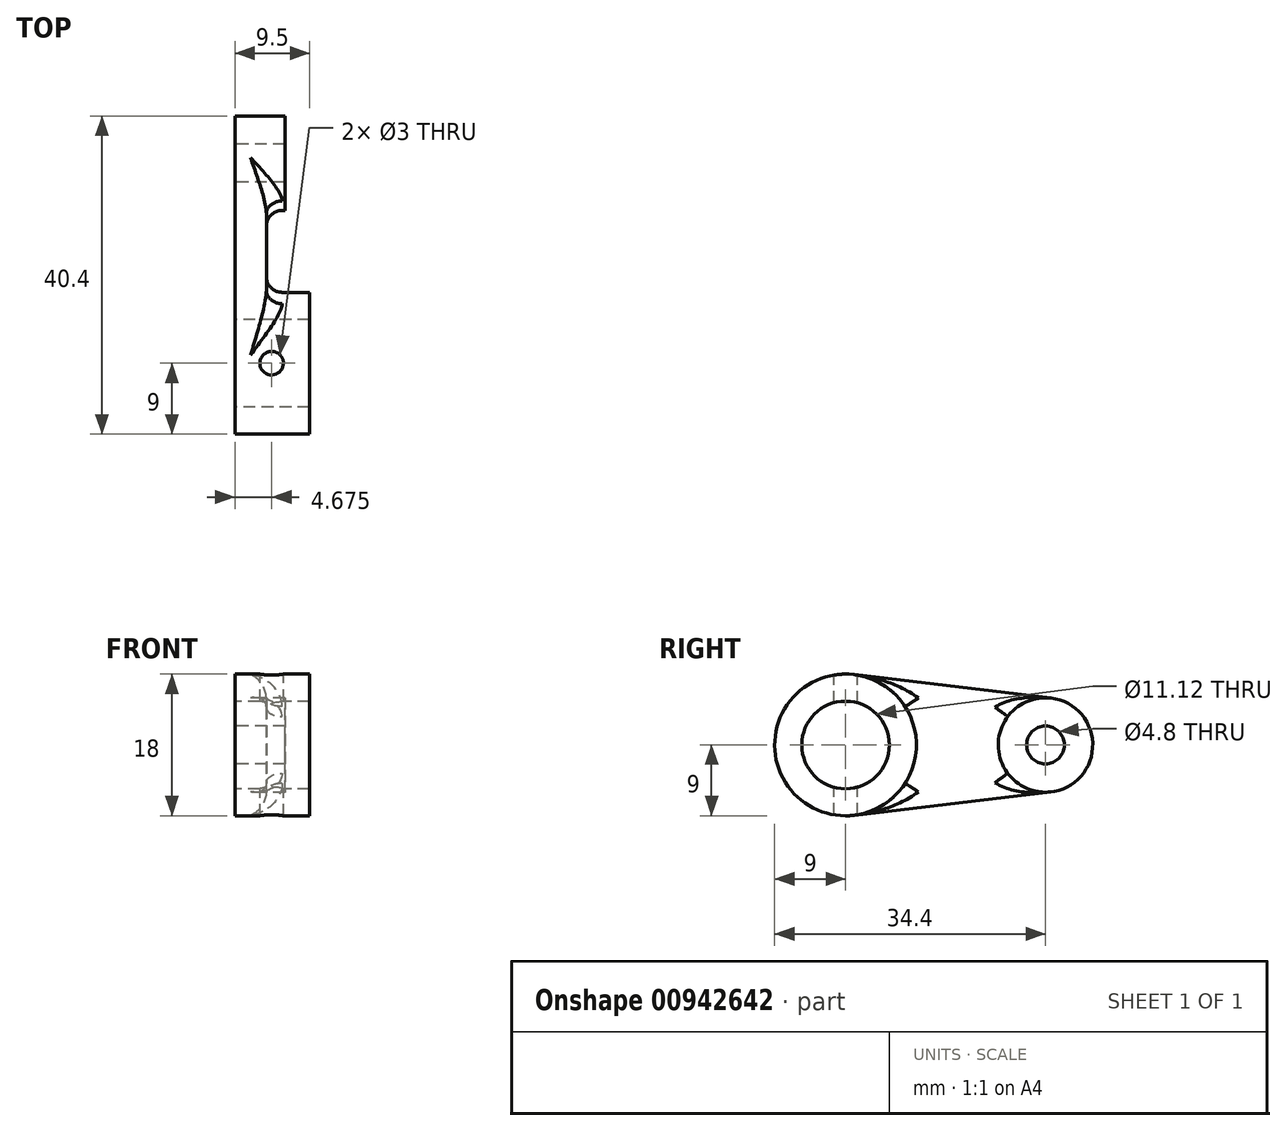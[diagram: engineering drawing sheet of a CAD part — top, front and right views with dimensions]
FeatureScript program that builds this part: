
annotation { "Feature Type Name" : "Feature", "Feature Type Description" : "" }
export const myFeature = defineFeature(function(context is Context, id is Id, definition is map)
    precondition{}
    {
        {
            var Q0;
            Q0=qCreatedBy(makeId("Right.planeOp"),FACE);
            var sketch = newSketch(context, id + "F0", { "sketchPlane" : qUnion([Q0])});
            skCircle(sketch, "E0", {"center": v(0, 0) * mm, "radius": 9 * mm});
            skCircle(sketch, "E1", {"center": v(0, 0) * mm, "radius": 5.56 * mm});
            skSolve(sketch);
        }
        {
            var Q0;
            Q0 = qSketchRegion(id + "F0", true);
            extrude(context, id + "F1", {"entities" : qUnion([Q0]), "depth" : 9.5 * mm, "offsetDistance" : 25 * mm});
        }
        {
            var Q0;
            Q0=qCreatedBy(makeId("Right.planeOp"),FACE);
            var sketch = newSketch(context, id + "F2", { "sketchPlane" : qUnion([Q0])});
            skCircle(sketch, "E2", {"center": v(25.4, 0) * mm, "radius": 6 * mm});
            skCircle(sketch, "E3", {"center": v(25.4, 0) * mm, "radius": 2.4 * mm});
            skSolve(sketch);
        }
        {
            var Q0;
            Q0 = qSketchRegion(id + "F2", true);
            extrude(context, id + "F3", {"entities" : qUnion([Q0]), "depth" : 6.35 * mm, "offsetDistance" : 25 * mm});
        }
        {
            var Q0;
            Q0=qCreatedBy(makeId("Right.planeOp"),FACE);
            var sketch = newSketch(context, id + "F4", { "sketchPlane" : qUnion([Q0])});
            skArc(sketch, "E4.0", {"start": v(1.06, -8.94) * mm, "mid": v(9, 0) * mm, "end": v(1.06, 8.94) * mm});
            skArc(sketch, "E5.0", {"start": v(26.1, 5.96) * mm, "mid": v(19.4, 0) * mm, "end": v(26.1, -5.96) * mm});
            skLineSegment(sketch, "E6", {"start": v(1.06, 8.94) * mm, "end": v(26.1, 5.96) * mm});
            skLineSegment(sketch, "E7", {"start": v(1.06, -8.94) * mm, "end": v(26.1, -5.96) * mm});
            skSolve(sketch);
        }
        {
            var Q0;
            Q0 = qSketchRegion(id + "F4", true);
            extrude(context, id + "F5", {"entities" : qUnion([Q0]), "operationType" : NewBodyOperationType.ADD, "depth" : 4 * mm, "offsetDistance" : 25 * mm});
        }
        {
            var Q0;
            Q0=makeQuery(id+"F5.opExtrude","CAP_FACE",FACE,{"disambiguationData":[OSD([sQuery(id+"F4.wireOp",EDGE,"E4.0"),sQuery(id+"F4.wireOp",EDGE,"E5.0"),sQuery(id+"F4.wireOp",EDGE,"E6"),sQuery(id+"F4.wireOp",EDGE,"E7")])],"isStart":false});
            fillet(context, id + "F6", {"entities" : qUnion([Q0]), "radius" : 2 * mm, "tangentPropagation" : true, "allowEdgeOverflow" : false});
        }
        {
            var Q0;
            Q0=qCreatedBy(makeId("Top.planeOp"),FACE);
            var sketch = newSketch(context, id + "F7", { "sketchPlane" : qUnion([Q0])});
            skCircle(sketch, "E8", {"center": v(4.68, 0) * mm, "radius": 1.5 * mm});
            skSolve(sketch);
        }
        {
            var Q0;
            Q0 = qSketchRegion(id + "F7", true);
            extrude(context, id + "F8", {"entities" : qUnion([Q0]), "operationType" : NewBodyOperationType.REMOVE, "endBound" : BoundingType.THROUGH_ALL, "oppositeDirection" : true, "depth" : 25 * mm, "offsetDistance" : 25 * mm, "hasSecondDirection" : true, "secondDirectionBound" : SecondDirectionBoundingType.THROUGH_ALL, "secondDirectionOppositeDirection" : false, "secondDirectionDepth" : 25 * mm});
        }
    });
